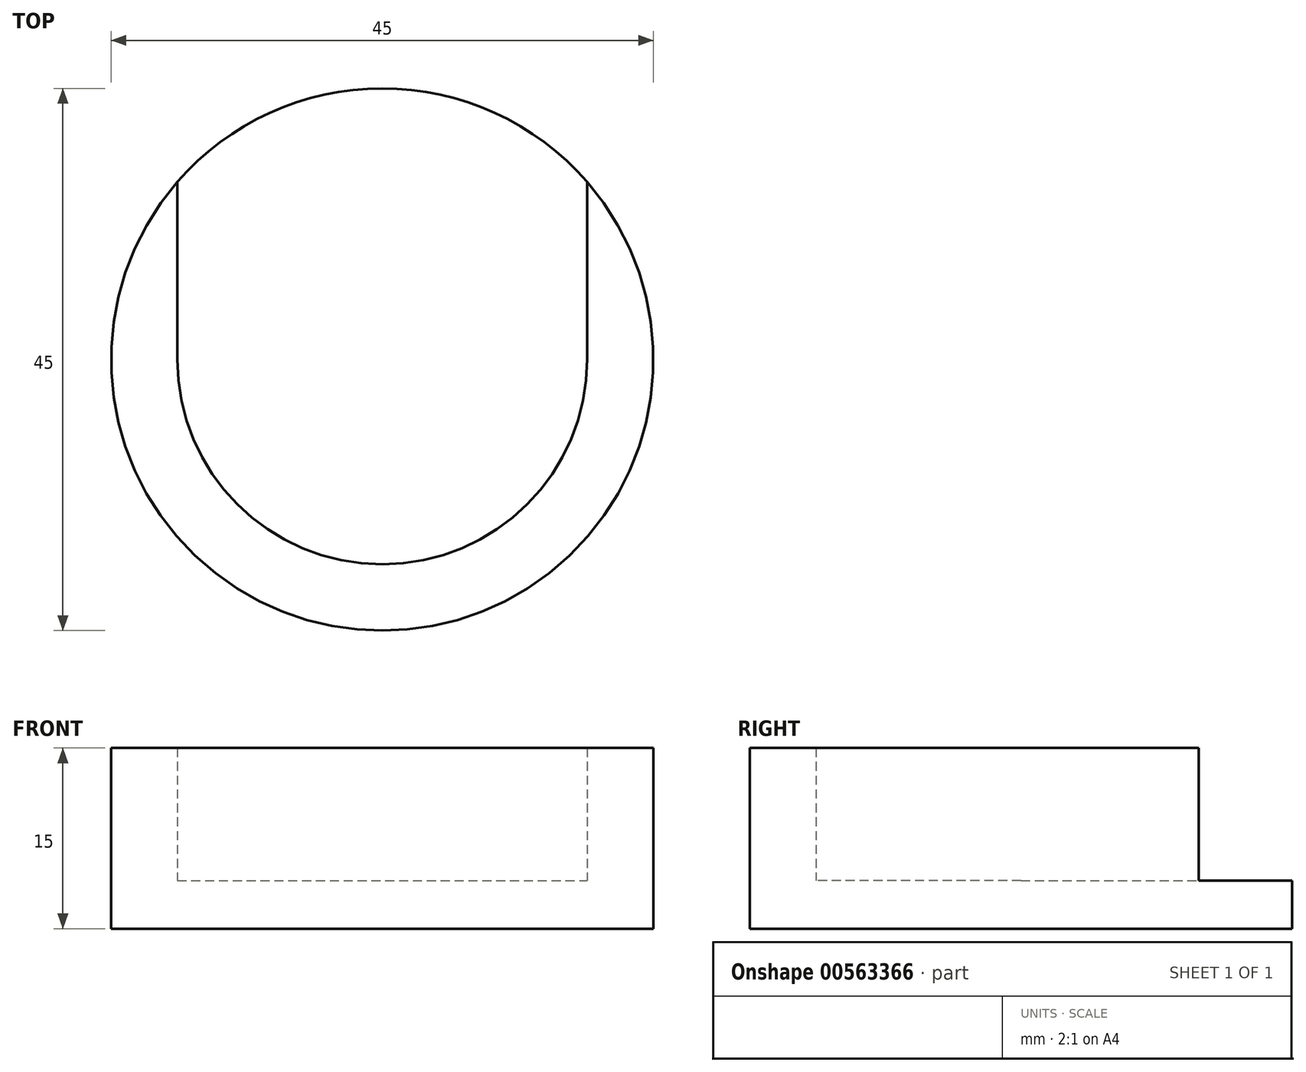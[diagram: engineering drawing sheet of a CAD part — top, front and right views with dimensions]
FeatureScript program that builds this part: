
annotation { "Feature Type Name" : "Feature", "Feature Type Description" : "" }
export const myFeature = defineFeature(function(context is Context, id is Id, definition is map)
    precondition{}
    {
        {
            var Q0;
            Q0=qCreatedBy(makeId("Top.planeOp"),FACE);
            var sketch = newSketch(context, id + "F0", { "sketchPlane" : qUnion([Q0])});
            skCircle(sketch, "E0", {"center": v(0, 0) * mm, "radius": 17 * mm});
            skCircle(sketch, "E1", {"center": v(0, 0) * mm, "radius": 22.5 * mm});
            skLineSegment(sketch, "E2", {"start": v(-22.5, 0) * mm, "end": v(22.5, 0) * mm});
            skLineSegment(sketch, "E3", {"start": v(17, 0) * mm, "end": v(17, 14.74) * mm});
            skLineSegment(sketch, "E4", {"start": v(-17, 0) * mm, "end": v(-17, 14.74) * mm});
            skSolve(sketch);
        }
        {
            var Q0;
            {var subQ0=sQuery(id+"F0.wireOp",EDGE,"E2");var subQ1=sQuery(id+"F0.wireOp",EDGE,"E0");var subQ2=makeQuery(id+"F0.imprint","INTERSECT",VERTEX,{"derivedFrom":[subQ1,subQ0,sQuery(id+"F0.wireOp",EDGE,"E3")]});Q0=makeQuery(id+"F0.imprint","IMPRINT",FACE,{"disambiguationData":[TD([[makeQuery(id+"F0.imprint","IMPRINT",EDGE,{"disambiguationData":[TD([[subQ2,1.0]])],"derivedFrom":subQ1}),-1.0]])]});}
            var Q1;
            {var subQ3=sQuery(id+"F0.wireOp",EDGE,"E4");Q1=makeQuery(id+"F0.imprint","IMPRINT",FACE,{"disambiguationData":[TD([[makeQuery(id+"F0.imprint","IMPRINT",EDGE,{"derivedFrom":subQ3}),1.0]])]});}
            var Q2;
            {var subQ3=sQuery(id+"F0.wireOp",EDGE,"E3");Q2=makeQuery(id+"F0.imprint","IMPRINT",FACE,{"disambiguationData":[TD([[makeQuery(id+"F0.imprint","IMPRINT",EDGE,{"derivedFrom":subQ3}),-1.0]])]});}
            extrude(context, id + "F1", {"entities" : qUnion([Q0, Q1, Q2]), "depth" : 15 * mm, "offsetDistance" : 25 * mm});
        }
        {
            var Q0;
            {var subQ0=sQuery(id+"F0.wireOp",EDGE,"E2");var subQ1=sQuery(id+"F0.wireOp",EDGE,"E0");var subQ2=makeQuery(id+"F0.imprint","INTERSECT",VERTEX,{"disambiguationData":[OD(0.0)],"derivedFrom":[subQ1,subQ0]});Q0=makeQuery(id+"F0.imprint","IMPRINT",FACE,{"disambiguationData":[TD([[makeQuery(id+"F0.imprint","IMPRINT",EDGE,{"disambiguationData":[TD([[subQ2,-1.0]])],"derivedFrom":subQ1}),1.0]])]});}
            var Q1;
            {var subQ0=sQuery(id+"F0.wireOp",EDGE,"E2");var subQ1=sQuery(id+"F0.wireOp",EDGE,"E0");var subQ2=makeQuery(id+"F0.imprint","INTERSECT",VERTEX,{"disambiguationData":[OD(0.0)],"derivedFrom":[subQ1,subQ0]});Q1=makeQuery(id+"F0.imprint","IMPRINT",FACE,{"disambiguationData":[TD([[makeQuery(id+"F0.imprint","IMPRINT",EDGE,{"disambiguationData":[TD([[subQ2,1.0]])],"derivedFrom":subQ1}),1.0]])]});}
            var Q2;
            Q2=makeQuery(id+"F0.imprint","IMPRINT",FACE,{"disambiguationData":[TD([[makeQuery(id+"F0.imprint","IMPRINT",EDGE,{"derivedFrom":sQuery(id+"F0.wireOp",EDGE,"ScDzBulV-GW5l-XsR5-KOqn-R5Fjek6Aud1x.top")}),-1.0]])]});
            var Q3;
            {var subQ0=sQuery(id+"F0.wireOp",EDGE,"E3");Q3=makeQuery(id+"F0.imprint","IMPRINT",FACE,{"disambiguationData":[TD([[makeQuery(id+"F0.imprint","IMPRINT",EDGE,{"derivedFrom":subQ0}),1.0]])]});}
            extrude(context, id + "F2", {"entities" : qUnion([Q0, Q1, Q2, Q3]), "operationType" : NewBodyOperationType.ADD, "depth" : 4 * mm, "offsetDistance" : 25 * mm});
        }
    });
